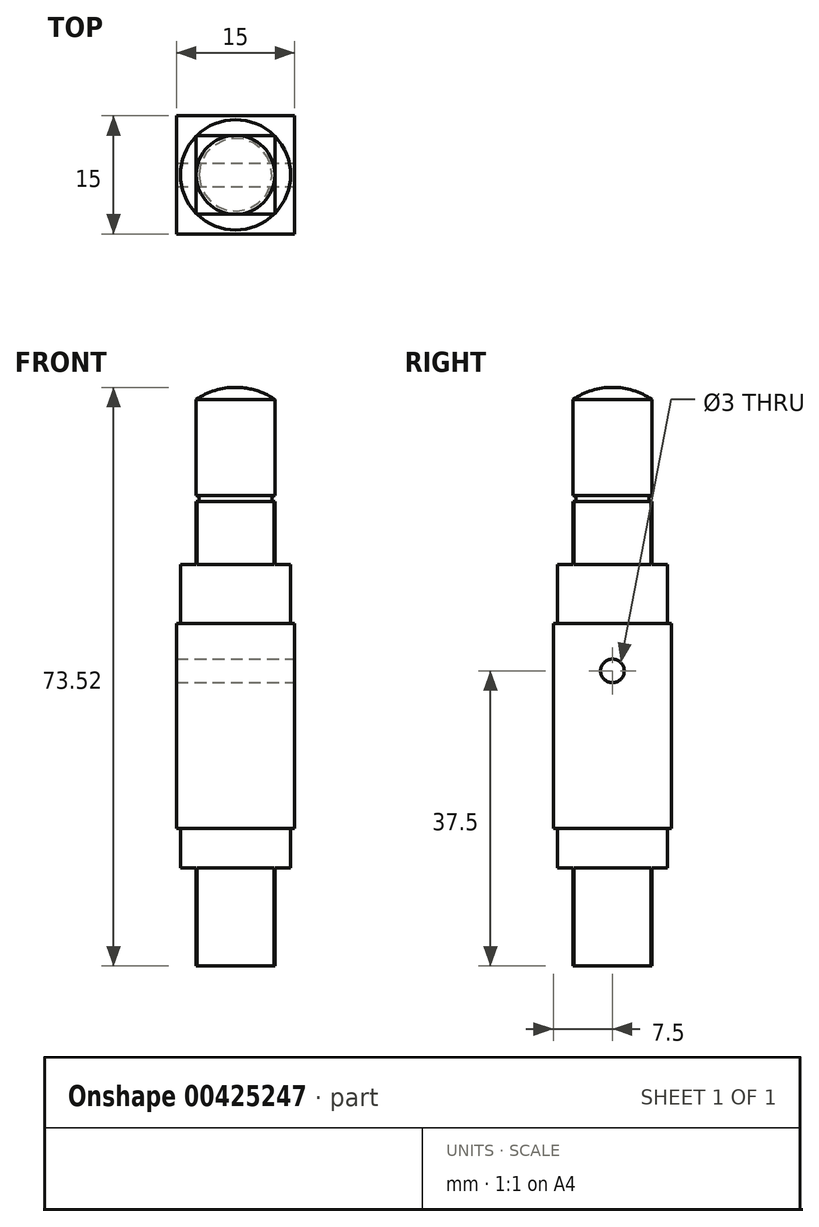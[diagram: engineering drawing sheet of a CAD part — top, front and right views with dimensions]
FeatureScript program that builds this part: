
annotation { "Feature Type Name" : "Feature", "Feature Type Description" : "" }
export const myFeature = defineFeature(function(context is Context, id is Id, definition is map)
    precondition{}
    {
        {
            var Q0;
            Q0=qCreatedBy(makeId("Top.planeOp"),FACE);
            var sketch = newSketch(context, id + "F0", { "sketchPlane" : qUnion([Q0])});
            skLineSegment(sketch, "E0.bottom", {"start": v(7.5, 7.5) * mm, "end": v(-7.5, 7.5) * mm});
            skLineSegment(sketch, "E0.top", {"start": v(7.5, -7.5) * mm, "end": v(-7.5, -7.5) * mm});
            skLineSegment(sketch, "E0.left", {"start": v(7.5, 7.5) * mm, "end": v(7.5, -7.5) * mm});
            skLineSegment(sketch, "E0.right", {"start": v(-7.5, 7.5) * mm, "end": v(-7.5, -7.5) * mm});
            skPoint(sketch, "E0.middle", {"position": v(0, 0) * mm});
            skSolve(sketch);
        }
        {
            var Q0;
            Q0 = qSketchRegion(id + "F0", true);
            extrude(context, id + "F1", {"entities" : qUnion([Q0]), "endBound" : BoundingType.SYMMETRIC, "depth" : (26) * mm});
        }
        {
            var Q0;
            Q0=makeQuery(id+"F1.opExtrude","CAP_FACE",FACE,{"disambiguationData":[OSD([sQuery(id+"F0.wireOp",EDGE,"E0.bottom"),sQuery(id+"F0.wireOp",EDGE,"E0.top"),sQuery(id+"F0.wireOp",EDGE,"E0.left"),sQuery(id+"F0.wireOp",EDGE,"E0.right")])],"isStart":true});
            var sketch = newSketch(context, id + "F2", { "sketchPlane" : qUnion([Q0])});
            skCircle(sketch, "E1", {"center": v(0, 0) * mm, "radius": 7 * mm});
            skSolve(sketch);
        }
        {
            var Q0;
            Q0=makeQuery(id+"F2.imprint","IMPRINT",FACE,{"disambiguationData":[TD([[makeQuery(id+"F2.imprint","IMPRINT",EDGE,{"derivedFrom":sQuery(id+"F2.wireOp",EDGE,"E1")}),1.0]])]});
            extrude(context, id + "F3", {"entities" : qUnion([Q0]), "operationType" : NewBodyOperationType.ADD, "depth" : 5 * mm});
        }
        {
            var Q0;
            Q0=makeQuery(id+"F3.opExtrude","CAP_FACE",FACE,{"disambiguationData":[OSD([sQuery(id+"F2.wireOp",EDGE,"E1")])],"isStart":false});
            var sketch = newSketch(context, id + "F4", { "sketchPlane" : qUnion([Q0])});
            skLineSegment(sketch, "E2.bottom", {"start": v(5, -5) * mm, "end": v(-5, -5) * mm});
            skLineSegment(sketch, "E2.top", {"start": v(5, 5) * mm, "end": v(-5, 5) * mm});
            skLineSegment(sketch, "E2.left", {"start": v(5, -5) * mm, "end": v(5, 5) * mm});
            skLineSegment(sketch, "E2.right", {"start": v(-5, -5) * mm, "end": v(-5, 5) * mm});
            skPoint(sketch, "E2.middle", {"position": v(0, 0) * mm});
            skSolve(sketch);
        }
        {
            var Q0;
            {var subQ1=makeQuery(id+"F3.opExtrude","CAP_EDGE",EDGE,{"disambiguationData":[OSD([sQuery(id+"F2.wireOp",EDGE,"E1")])],"isStart":false});var subQ10=sQuery(id+"F4.wireOp",EDGE,"E2.bottom");var subQ11=makeQuery(id+"F4.imprint","INTERSECT",VERTEX,{"disambiguationData":[OD(0.0)],"derivedFrom":[subQ1,subQ10]});Q0=makeQuery(id+"F4.imprint","IMPRINT",FACE,{"disambiguationData":[TD([[makeQuery(id+"F4.imprint","IMPRINT",EDGE,{"disambiguationData":[TD([[subQ11,-1.0]])],"derivedFrom":subQ10}),-1.0]])]});}
            extrude(context, id + "F5", {"entities" : qUnion([Q0]), "operationType" : NewBodyOperationType.ADD, "depth" : 12.5 * mm});
        }
        {
            var Q0;
            Q0=makeQuery(id+"F1.opExtrude","CAP_FACE",FACE,{"disambiguationData":[OSD([sQuery(id+"F0.wireOp",EDGE,"E0.bottom"),sQuery(id+"F0.wireOp",EDGE,"E0.top"),sQuery(id+"F0.wireOp",EDGE,"E0.left"),sQuery(id+"F0.wireOp",EDGE,"E0.right")])],"isStart":false});
            var sketch = newSketch(context, id + "F6", { "sketchPlane" : qUnion([Q0])});
            skCircle(sketch, "E3", {"center": v(0, 0) * mm, "radius": 7 * mm});
            skSolve(sketch);
        }
        {
            var Q0;
            Q0=makeQuery(id+"F6.imprint","IMPRINT",FACE,{"disambiguationData":[TD([[makeQuery(id+"F6.imprint","IMPRINT",EDGE,{"derivedFrom":sQuery(id+"F6.wireOp",EDGE,"E3")}),1.0]])]});
            extrude(context, id + "F7", {"entities" : qUnion([Q0]), "operationType" : NewBodyOperationType.ADD, "depth" : 7.5 * mm});
        }
        {
            var Q0;
            Q0=makeQuery(id+"F7.opExtrude","CAP_FACE",FACE,{"disambiguationData":[OSD([sQuery(id+"F6.wireOp",EDGE,"E3")])],"isStart":false});
            var sketch = newSketch(context, id + "F8", { "sketchPlane" : qUnion([Q0])});
            skLineSegment(sketch, "E4.bottom", {"start": v(5, -5) * mm, "end": v(-5, -5) * mm});
            skLineSegment(sketch, "E4.top", {"start": v(5, 5) * mm, "end": v(-5, 5) * mm});
            skLineSegment(sketch, "E4.left", {"start": v(5, -5) * mm, "end": v(5, 5) * mm});
            skLineSegment(sketch, "E4.right", {"start": v(-5, -5) * mm, "end": v(-5, 5) * mm});
            skPoint(sketch, "E4.middle", {"position": v(0, 0) * mm});
            skSolve(sketch);
        }
        {
            var Q0;
            {var subQ1=makeQuery(id+"F7.opExtrude","CAP_EDGE",EDGE,{"disambiguationData":[OSD([sQuery(id+"F6.wireOp",EDGE,"E3")])],"isStart":false});var subQ10=sQuery(id+"F8.wireOp",EDGE,"E4.bottom");var subQ11=makeQuery(id+"F8.imprint","INTERSECT",VERTEX,{"disambiguationData":[OD(0.0)],"derivedFrom":[subQ1,subQ10]});Q0=makeQuery(id+"F8.imprint","IMPRINT",FACE,{"disambiguationData":[TD([[makeQuery(id+"F8.imprint","IMPRINT",EDGE,{"disambiguationData":[TD([[subQ11,-1.0]])],"derivedFrom":subQ10}),-1.0]])]});}
            extrude(context, id + "F9", {"entities" : qUnion([Q0]), "operationType" : NewBodyOperationType.ADD, "depth" : 8 * mm});
        }
        {
            var Q0;
            Q0=makeQuery(id+"F9.opExtrude","CAP_FACE",FACE,{"disambiguationData":[OSD([sQuery(id+"F6.wireOp",EDGE,"E3"),sQuery(id+"F8.wireOp",EDGE,"E4.bottom"),sQuery(id+"F8.wireOp",EDGE,"E4.top"),sQuery(id+"F8.wireOp",EDGE,"E4.left"),sQuery(id+"F8.wireOp",EDGE,"E4.right")])],"isStart":false});
            var sketch = newSketch(context, id + "F10", { "sketchPlane" : qUnion([Q0])});
            skCircle(sketch, "E5", {"center": v(0, 0) * mm, "radius": 5 * mm});
            skSolve(sketch);
        }
        {
            var Q0;
            Q0 = qSketchRegion(id + "F10", true);
            extrude(context, id + "F11", {"entities" : qUnion([Q0]), "operationType" : NewBodyOperationType.ADD, "depth" : 13 * mm});
        }
        {
            var Q0;
            Q0=qCreatedBy(makeId("Right.planeOp"),FACE);
            var sketch = newSketch(context, id + "F12", { "sketchPlane" : qUnion([Q0])});
            skArc(sketch, "E6", {"start": v(5, 29.25) * mm, "mid": v(4.62, 28.88) * mm, "end": v(5, 28.5) * mm});
            skLineSegment(sketch, "E7", {"start": v(5, 29.25) * mm, "end": v(5, 28.5) * mm});
            skSolve(sketch);
        }
        {
            var Q0;
            Q0 = qSketchRegion(id + "F12", true);
            var Q1;
            Q1=makeQuery(id+"F11.opExtrude","SWEPT_FACE",FACE,{"disambiguationData":[OSD([sQuery(id+"F10.wireOp",EDGE,"E5")])]});
            revolve(context, id + "F13", {"operationType" : NewBodyOperationType.REMOVE, "entities" : qUnion([Q0]), "axis" : qUnion([Q1]), "revolveType" : RevolveType.FULL, "oppositeDirection" : true});
        }
        {
            var Q0;
            Q0=qCreatedBy(makeId("Front.planeOp"),FACE);
            var sketch = newSketch(context, id + "F14", { "sketchPlane" : qUnion([Q0])});
            skArc(sketch, "E8", {"start": v(5, 41.5) * mm, "mid": v(2.61, 42.63) * mm, "end": v(0, 43.02) * mm});
            skLineSegment(sketch, "E9", {"start": v(0, 43.02) * mm, "end": v(0, 41.5) * mm});
            skLineSegment(sketch, "E10", {"start": v(0, 41.5) * mm, "end": v(5, 41.5) * mm});
            skSolve(sketch);
        }
        {
            var Q0;
            Q0=makeQuery(id+"F14.imprint","IMPRINT",FACE,{"disambiguationData":[TD([[makeQuery(id+"F14.imprint","IMPRINT",EDGE,{"derivedFrom":sQuery(id+"F14.wireOp",EDGE,"E8")}),1.0]])]});
            var Q1;
            Q1=makeQuery(id+"F11.opExtrude","CAP_EDGE",EDGE,{"disambiguationData":[OSD([sQuery(id+"F10.wireOp",EDGE,"E5")])],"isStart":false});
            revolve(context, id + "F15", {"operationType" : NewBodyOperationType.ADD, "entities" : qUnion([Q0]), "axis" : qUnion([Q1]), "revolveType" : RevolveType.FULL});
        }
        {
            var Q0;
            Q0=makeQuery(id+"F1.opExtrude","SWEPT_FACE",FACE,{"disambiguationData":[OSD([sQuery(id+"F0.wireOp",EDGE,"E0.left")])]});
            var sketch = newSketch(context, id + "F16", { "sketchPlane" : qUnion([Q0])});
            skCircle(sketch, "E11", {"center": v(0, 7) * mm, "radius": 1.5 * mm});
            skSolve(sketch);
        }
        {
            var Q0;
            Q0=makeQuery(id+"F16.imprint","IMPRINT",FACE,{"disambiguationData":[TD([[makeQuery(id+"F16.imprint","IMPRINT",EDGE,{"derivedFrom":sQuery(id+"F16.wireOp",EDGE,"E11")}),1.0]])]});
            extrude(context, id + "F17", {"entities" : qUnion([Q0]), "operationType" : NewBodyOperationType.REMOVE, "oppositeDirection" : true, "depth" : 25 * mm});
        }
    });
